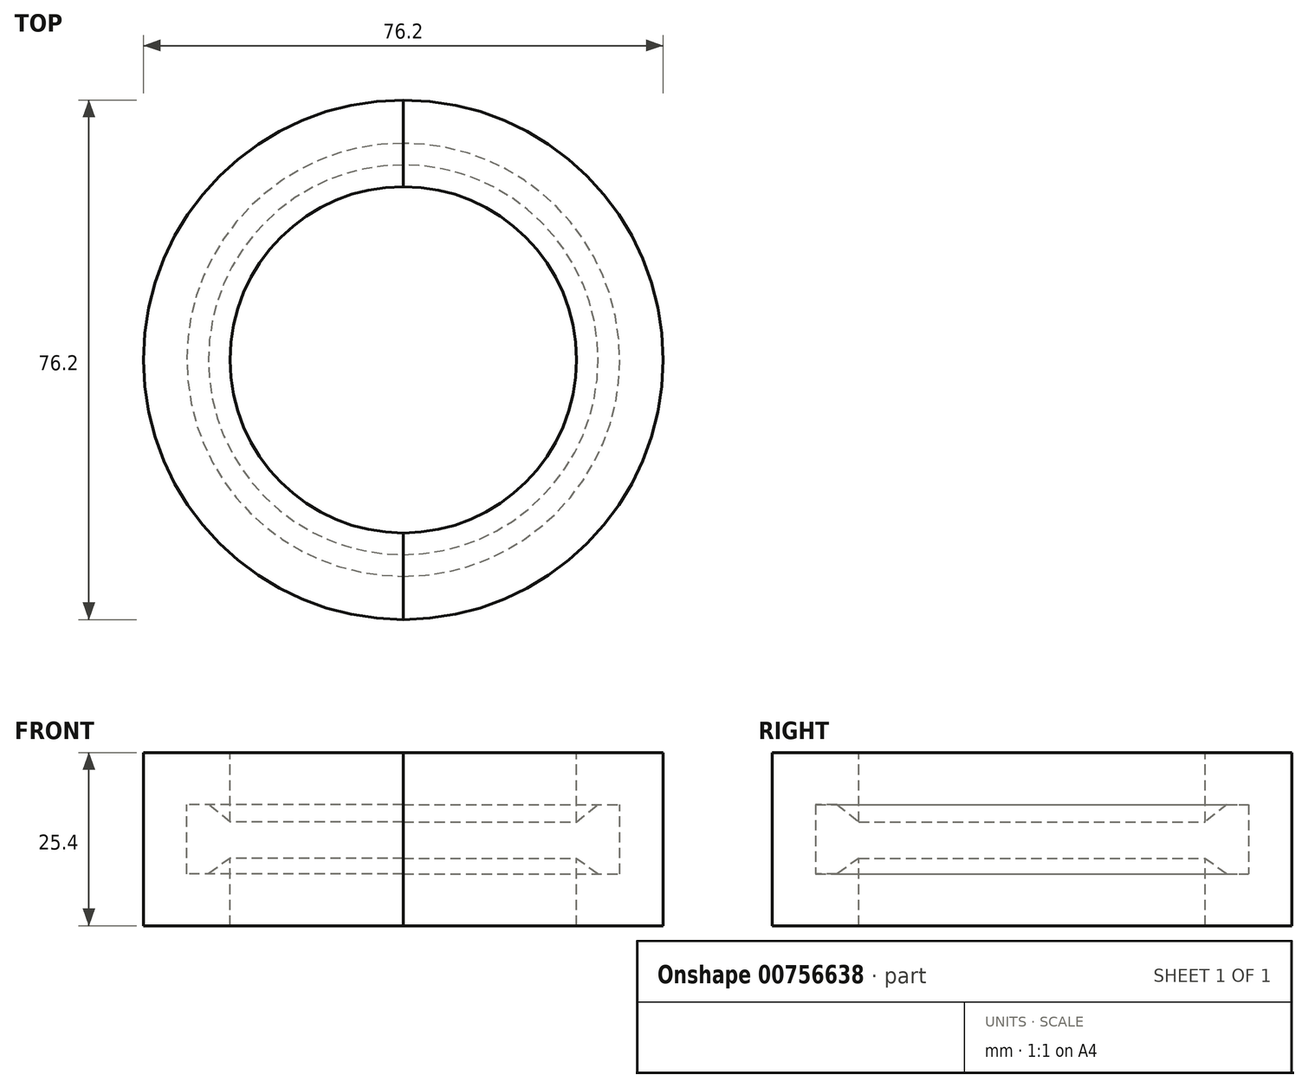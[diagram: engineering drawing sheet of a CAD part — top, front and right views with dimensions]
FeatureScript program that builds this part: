
annotation { "Feature Type Name" : "Feature", "Feature Type Description" : "" }
export const myFeature = defineFeature(function(context is Context, id is Id, definition is map)
    precondition{}
    {
        {
            var Q0;
            Q0=qCreatedBy(makeId("Front.planeOp"),FACE);
            var sketch = newSketch(context, id + "F0", { "sketchPlane" : qUnion([Q0])});
            skLineSegment(sketch, "E0.bottom", {"start": v(25.4, -12.7) * mm, "end": v(38.1, -12.7) * mm});
            skLineSegment(sketch, "E0.top", {"start": v(25.4, 12.7) * mm, "end": v(38.1, 12.7) * mm});
            skLineSegment(sketch, "E0.left", {"start": v(25.4, -12.7) * mm, "end": v(25.4, -2.8) * mm});
            skLineSegment(sketch, "E0.right", {"start": v(38.1, -12.7) * mm, "end": v(38.1, 12.7) * mm});
            skLineSegment(sketch, "E1", {"start": v(25.4, -2.8) * mm, "end": v(28.58, -5.08) * mm});
            skLineSegment(sketch, "E2", {"start": v(28.58, 5.08) * mm, "end": v(25.4, 2.54) * mm});
            skLineSegment(sketch, "E3", {"start": v(0, 9.64) * mm, "end": v(0, -7.88) * mm, "construction": true});
            skLineSegment(sketch, "E4.trimOffspring", {"start": v(25.4, 2.54) * mm, "end": v(25.4, 12.7) * mm});
            skLineSegment(sketch, "E5.bottom", {"start": v(28.58, 5.08) * mm, "end": v(31.75, 5.08) * mm});
            skLineSegment(sketch, "E5.top", {"start": v(28.58, -5.08) * mm, "end": v(31.75, -5.08) * mm});
            skLineSegment(sketch, "E5.right", {"start": v(31.75, 5.08) * mm, "end": v(31.75, -5.08) * mm});
            skSolve(sketch);
        }
        {
            var Q0;
            Q0 = qSketchRegion(id + "F0", true);
            var Q1;
            Q1=sQuery(id+"F0.wireOp",EDGE,"E3");
            revolve(context, id + "F1", {"surfaceOperationType" : NewSurfaceOperationType.NEW, "entities" : qUnion([Q0]), "axis" : qUnion([Q1]), "revolveType" : RevolveType.SYMMETRIC, "angle" : 180 * degree});
        }
        {
            var Q0;
            Q0=makeQuery(id+"F1.opRevolve","SWEPT_BODY",BODY,{"disambiguationData":[OSD([sQuery(id+"F0.wireOp",EDGE,"E0.bottom"),sQuery(id+"F0.wireOp",EDGE,"E0.top"),sQuery(id+"F0.wireOp",EDGE,"E0.left"),sQuery(id+"F0.wireOp",EDGE,"E0.right"),sQuery(id+"F0.wireOp",EDGE,"E1"),sQuery(id+"F0.wireOp",EDGE,"eYa51NgK-KXzU-7XyA-87gw-XXz1BnMRks3d"),sQuery(id+"F0.wireOp",EDGE,"E2"),sQuery(id+"F0.wireOp",EDGE,"E4.trimOffspring")])]});
            var Q1;
            Q1=qCreatedBy(makeId("Right.planeOp"),FACE);
            mirror(context, id + "F2", {"entities" : qUnion([Q0]), "mirrorPlane" : qUnion([Q1])});
        }
    });
